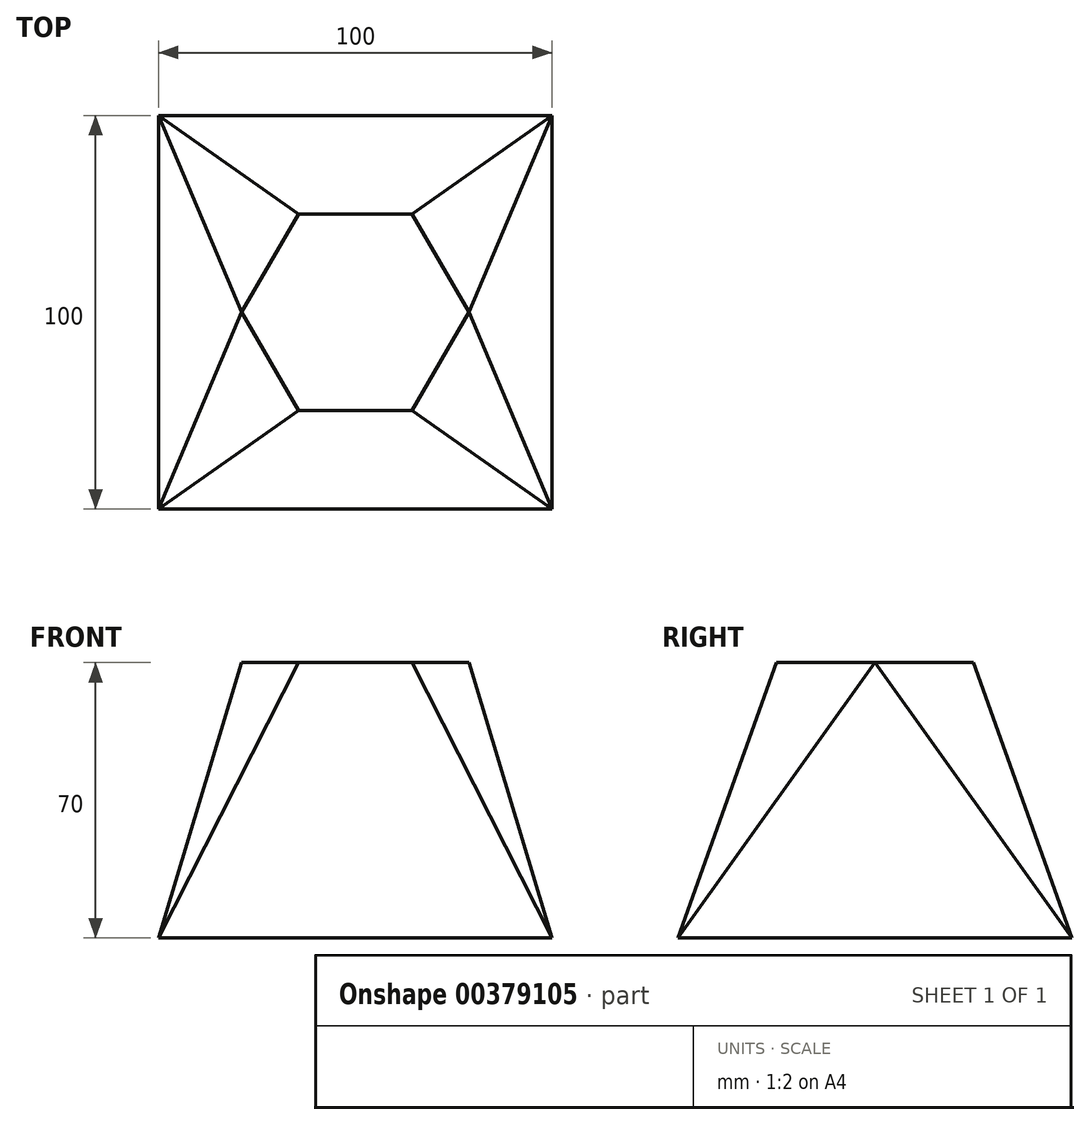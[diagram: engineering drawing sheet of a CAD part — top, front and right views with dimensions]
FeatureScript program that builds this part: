
annotation { "Feature Type Name" : "Feature", "Feature Type Description" : "" }
export const myFeature = defineFeature(function(context is Context, id is Id, definition is map)
    precondition{}
    {
        {
            var Q0;
            Q0=qCreatedBy(makeId("Top.planeOp"),FACE);
            var sketch = newSketch(context, id + "F0", { "sketchPlane" : qUnion([Q0])});
            skLineSegment(sketch, "E0.bottom", {"start": v(50, 50) * mm, "end": v(-50, 50) * mm});
            skLineSegment(sketch, "E0.top", {"start": v(50, -50) * mm, "end": v(-50, -50) * mm});
            skLineSegment(sketch, "E0.left", {"start": v(50, 50) * mm, "end": v(50, -50) * mm});
            skLineSegment(sketch, "E0.right", {"start": v(-50, 50) * mm, "end": v(-50, -50) * mm});
            skPoint(sketch, "E0.middle", {"position": v(0, 0) * mm});
            skSolve(sketch);
        }
        {
            var Q0;
            Q0=qCreatedBy(makeId("Top.planeOp"),FACE);
            cPlane(context, id + "F1", {"entities" : qUnion([Q0]), "cplaneType" : CPlaneType.OFFSET, "offset" : 70 * mm, "width" : 150 * mm, "height" : 150 * mm});
        }
        {
            var Q0;
            Q0=qCreatedBy(id+"F1.planeOp",FACE);
            var sketch = newSketch(context, id + "F2", { "sketchPlane" : qUnion([Q0])});
            skCircle(sketch, "E1.cCircle", {"center": v(0, 0) * mm, "radius": 28.87 * mm, "construction": true});
            skLineSegment(sketch, "E1.0", {"start": v(28.87, 0) * mm, "end": v(14.43, -25) * mm});
            skLineSegment(sketch, "E1.1", {"start": v(14.43, -25) * mm, "end": v(-14.43, -25) * mm});
            skLineSegment(sketch, "E1.2", {"start": v(-14.43, -25) * mm, "end": v(-28.87, 0) * mm});
            skLineSegment(sketch, "E1.3", {"start": v(-28.87, 0) * mm, "end": v(-14.43, 25) * mm});
            skLineSegment(sketch, "E1.4", {"start": v(-14.43, 25) * mm, "end": v(14.43, 25) * mm});
            skLineSegment(sketch, "E1.5", {"start": v(14.43, 25) * mm, "end": v(28.87, 0) * mm});
            skLineSegment(sketch, "E2", {"start": v(28.87, 25) * mm, "end": v(14.43, 25) * mm});
            skLineSegment(sketch, "E3", {"start": v(28.87, 0) * mm, "end": v(28.87, 25) * mm});
            skSolve(sketch);
        }
        {
            var Q0;
            Q0=qCreatedBy(id+"F1.planeOp",FACE);
            var sketch = newSketch(context, id + "F3", { "sketchPlane" : qUnion([Q0])});
            skLineSegment(sketch, "E4.bottom", {"start": v(28.87, 25) * mm, "end": v(-28.87, 25) * mm});
            skLineSegment(sketch, "E4.top", {"start": v(28.87, -25) * mm, "end": v(-28.87, -25) * mm});
            skLineSegment(sketch, "E4.left", {"start": v(28.87, 25) * mm, "end": v(28.87, -25) * mm});
            skLineSegment(sketch, "E4.right", {"start": v(-28.87, 25) * mm, "end": v(-28.87, -25) * mm});
            skPoint(sketch, "E4.middle", {"position": v(0, 0) * mm});
            skSolve(sketch);
        }
        {
            var Q0;
            Q0=makeQuery(id+"F3.imprint","IMPRINT",FACE,{"disambiguationData":[TD([[makeQuery(id+"F3.imprint","IMPRINT",EDGE,{"derivedFrom":sQuery(id+"F3.wireOp",EDGE,"E4.bottom")}),1.0]])]});
            var Q1;
            Q1=makeQuery(id+"F0.imprint","IMPRINT",FACE,{"disambiguationData":[TD([[makeQuery(id+"F0.imprint","IMPRINT",EDGE,{"derivedFrom":sQuery(id+"F0.wireOp",EDGE,"E0.bottom")}),1.0]])]});
            loft(context, id + "F4", {"sheetProfilesArray" : [{ "sheetProfileEntities" : qUnion([Q0]) }, { "sheetProfileEntities" : qUnion([Q1]) }]});
        }
        {
            var Q1;
            Q1=makeQuery(id+"F2.imprint","IMPRINT",FACE,{"disambiguationData":[TD([[makeQuery(id+"F2.imprint","IMPRINT",EDGE,{"derivedFrom":sQuery(id+"F2.wireOp",EDGE,"E1.5")}),1.0]])]});
            var Q2;
            Q2=makeQuery(id+"F4.opLoft","MID_CAP_VERTEX",VERTEX,{"disambiguationData":[OSD([sQuery(id+"F0.wireOp",EDGE,"E0.bottom"),sQuery(id+"F0.wireOp",EDGE,"E0.left")])],"capPos":1.0});
            loft(context, id + "F5", {"sheetProfilesArray" : [{ "sheetProfileEntities" : qUnion([Q1]) }, { "sheetProfileEntities" : qUnion([Q2]) }]});
        }
        {
            var Q0;
            Q0=makeQuery(id+"F5.opLoft","SWEPT_BODY",BODY,{"disambiguationData":[OSD([sQuery(id+"F0.wireOp",EDGE,"E0.bottom"),sQuery(id+"F0.wireOp",EDGE,"E0.left"),makeQuery(id+"F2.imprint","IMPRINT",FACE,{"disambiguationData":[TD([[makeQuery(id+"F2.imprint","IMPRINT",EDGE,{"derivedFrom":sQuery(id+"F2.wireOp",EDGE,"E1.5")}),1.0]])]})])]});
            var Q1;
            Q1=qCreatedBy(makeId("Front.planeOp"),FACE);
            mirror(context, id + "F6", {"entities" : qUnion([Q0]), "mirrorPlane" : qUnion([Q1])});
        }
        {
            var Q0;
            Q0=makeQuery(id+"F5.opLoft","SWEPT_BODY",BODY,{"disambiguationData":[OSD([sQuery(id+"F0.wireOp",EDGE,"E0.bottom"),sQuery(id+"F0.wireOp",EDGE,"E0.left"),makeQuery(id+"F2.imprint","IMPRINT",FACE,{"disambiguationData":[TD([[makeQuery(id+"F2.imprint","IMPRINT",EDGE,{"derivedFrom":sQuery(id+"F2.wireOp",EDGE,"E1.5")}),1.0]])]})])]});
            var Q1;
            Q1=makeQuery(id+"F6.opPattern","COPY",BODY,{"derivedFrom":makeQuery(id+"F5.opLoft","SWEPT_BODY",BODY,{"disambiguationData":[OSD([sQuery(id+"F0.wireOp",EDGE,"E0.bottom"),sQuery(id+"F0.wireOp",EDGE,"E0.left"),makeQuery(id+"F2.imprint","IMPRINT",FACE,{"disambiguationData":[TD([[makeQuery(id+"F2.imprint","IMPRINT",EDGE,{"derivedFrom":sQuery(id+"F2.wireOp",EDGE,"E1.5")}),1.0]])]})])]}),"instanceName":"1"});
            var Q2;
            Q2=qCreatedBy(makeId("Front.planeOp"),FACE);
            mirror(context, id + "F7", {"entities" : qUnion([Q0, Q1]), "mirrorPlane" : qUnion([Q2])});
        }
        {
            var Q0;
            Q0=makeQuery(id+"F7.opPattern","COPY",BODY,{"derivedFrom":makeQuery(id+"F6.opPattern","COPY",BODY,{"derivedFrom":makeQuery(id+"F5.opLoft","SWEPT_BODY",BODY,{"disambiguationData":[OSD([sQuery(id+"F0.wireOp",EDGE,"E0.bottom"),sQuery(id+"F0.wireOp",EDGE,"E0.left"),makeQuery(id+"F2.imprint","IMPRINT",FACE,{"disambiguationData":[TD([[makeQuery(id+"F2.imprint","IMPRINT",EDGE,{"derivedFrom":sQuery(id+"F2.wireOp",EDGE,"E1.5")}),1.0]])]})])]}),"instanceName":"1"}),"instanceName":"1"});
            var Q1;
            Q1=makeQuery(id+"F7.opPattern","COPY",BODY,{"derivedFrom":makeQuery(id+"F5.opLoft","SWEPT_BODY",BODY,{"disambiguationData":[OSD([sQuery(id+"F0.wireOp",EDGE,"E0.bottom"),sQuery(id+"F0.wireOp",EDGE,"E0.left"),makeQuery(id+"F2.imprint","IMPRINT",FACE,{"disambiguationData":[TD([[makeQuery(id+"F2.imprint","IMPRINT",EDGE,{"derivedFrom":sQuery(id+"F2.wireOp",EDGE,"E1.5")}),1.0]])]})])]}),"instanceName":"1"});
            var Q2;
            Q2=qCreatedBy(makeId("Right.planeOp"),FACE);
            mirror(context, id + "F8", {"entities" : qUnion([Q0, Q1]), "mirrorPlane" : qUnion([Q2])});
        }
        {
            var Q0;
            Q0=makeQuery(id+"F8.opPattern","COPY",BODY,{"derivedFrom":makeQuery(id+"F7.opPattern","COPY",BODY,{"derivedFrom":makeQuery(id+"F6.opPattern","COPY",BODY,{"derivedFrom":makeQuery(id+"F5.opLoft","SWEPT_BODY",BODY,{"disambiguationData":[OSD([sQuery(id+"F0.wireOp",EDGE,"E0.bottom"),sQuery(id+"F0.wireOp",EDGE,"E0.left"),makeQuery(id+"F2.imprint","IMPRINT",FACE,{"disambiguationData":[TD([[makeQuery(id+"F2.imprint","IMPRINT",EDGE,{"derivedFrom":sQuery(id+"F2.wireOp",EDGE,"E1.5")}),1.0]])]})])]}),"instanceName":"1"}),"instanceName":"1"}),"instanceName":"1"});
            var Q1;
            Q1=makeQuery(id+"F8.opPattern","COPY",BODY,{"derivedFrom":makeQuery(id+"F7.opPattern","COPY",BODY,{"derivedFrom":makeQuery(id+"F5.opLoft","SWEPT_BODY",BODY,{"disambiguationData":[OSD([sQuery(id+"F0.wireOp",EDGE,"E0.bottom"),sQuery(id+"F0.wireOp",EDGE,"E0.left"),makeQuery(id+"F2.imprint","IMPRINT",FACE,{"disambiguationData":[TD([[makeQuery(id+"F2.imprint","IMPRINT",EDGE,{"derivedFrom":sQuery(id+"F2.wireOp",EDGE,"E1.5")}),1.0]])]})])]}),"instanceName":"1"}),"instanceName":"1"});
            var Q2;
            Q2=makeQuery(id+"F6.opPattern","COPY",BODY,{"derivedFrom":makeQuery(id+"F5.opLoft","SWEPT_BODY",BODY,{"disambiguationData":[OSD([sQuery(id+"F0.wireOp",EDGE,"E0.bottom"),sQuery(id+"F0.wireOp",EDGE,"E0.left"),makeQuery(id+"F2.imprint","IMPRINT",FACE,{"disambiguationData":[TD([[makeQuery(id+"F2.imprint","IMPRINT",EDGE,{"derivedFrom":sQuery(id+"F2.wireOp",EDGE,"E1.5")}),1.0]])]})])]}),"instanceName":"1"});
            var Q3;
            Q3=makeQuery(id+"F5.opLoft","SWEPT_BODY",BODY,{"disambiguationData":[OSD([sQuery(id+"F0.wireOp",EDGE,"E0.bottom"),sQuery(id+"F0.wireOp",EDGE,"E0.left"),makeQuery(id+"F2.imprint","IMPRINT",FACE,{"disambiguationData":[TD([[makeQuery(id+"F2.imprint","IMPRINT",EDGE,{"derivedFrom":sQuery(id+"F2.wireOp",EDGE,"E1.5")}),1.0]])]})])]});
            var Q4;
            Q4=makeQuery(id+"F4.opLoft","SWEPT_BODY",BODY,{"disambiguationData":[OSD([makeQuery(id+"F0.imprint","IMPRINT",FACE,{"disambiguationData":[TD([[makeQuery(id+"F0.imprint","IMPRINT",EDGE,{"derivedFrom":sQuery(id+"F0.wireOp",EDGE,"E0.bottom")}),1.0]])]}),makeQuery(id+"F3.imprint","IMPRINT",FACE,{"disambiguationData":[TD([[makeQuery(id+"F3.imprint","IMPRINT",EDGE,{"derivedFrom":sQuery(id+"F3.wireOp",EDGE,"E4.bottom")}),1.0]])]})])]});
            booleanBodies(context, id + "F9", {"operationType" : BooleanOperationType.SUBTRACTION, "tools" : qUnion([Q0, Q1, Q2, Q3]), "targets" : qUnion([Q4])});
        }
        {
            var Q0;
            Q0=makeQuery(id+"F7.opPattern","COPY",BODY,{"derivedFrom":makeQuery(id+"F6.opPattern","COPY",BODY,{"derivedFrom":makeQuery(id+"F5.opLoft","SWEPT_BODY",BODY,{"disambiguationData":[OSD([sQuery(id+"F0.wireOp",EDGE,"E0.bottom"),sQuery(id+"F0.wireOp",EDGE,"E0.left"),makeQuery(id+"F2.imprint","IMPRINT",FACE,{"disambiguationData":[TD([[makeQuery(id+"F2.imprint","IMPRINT",EDGE,{"derivedFrom":sQuery(id+"F2.wireOp",EDGE,"E1.5")}),1.0]])]})])]}),"instanceName":"1"}),"instanceName":"1"});
            var Q1;
            Q1=makeQuery(id+"F7.opPattern","COPY",BODY,{"derivedFrom":makeQuery(id+"F5.opLoft","SWEPT_BODY",BODY,{"disambiguationData":[OSD([sQuery(id+"F0.wireOp",EDGE,"E0.bottom"),sQuery(id+"F0.wireOp",EDGE,"E0.left"),makeQuery(id+"F2.imprint","IMPRINT",FACE,{"disambiguationData":[TD([[makeQuery(id+"F2.imprint","IMPRINT",EDGE,{"derivedFrom":sQuery(id+"F2.wireOp",EDGE,"E1.5")}),1.0]])]})])]}),"instanceName":"1"});
            var Q2;
            Q2=makeQuery(id+"F4.opLoft","SWEPT_BODY",BODY,{"disambiguationData":[OSD([makeQuery(id+"F0.imprint","IMPRINT",FACE,{"disambiguationData":[TD([[makeQuery(id+"F0.imprint","IMPRINT",EDGE,{"derivedFrom":sQuery(id+"F0.wireOp",EDGE,"E0.bottom")}),1.0]])]}),makeQuery(id+"F3.imprint","IMPRINT",FACE,{"disambiguationData":[TD([[makeQuery(id+"F3.imprint","IMPRINT",EDGE,{"derivedFrom":sQuery(id+"F3.wireOp",EDGE,"E4.bottom")}),1.0]])]})])]});
            booleanBodies(context, id + "F10", {"operationType" : BooleanOperationType.SUBTRACTION, "tools" : qUnion([Q0, Q1]), "targets" : qUnion([Q2])});
        }
    });
